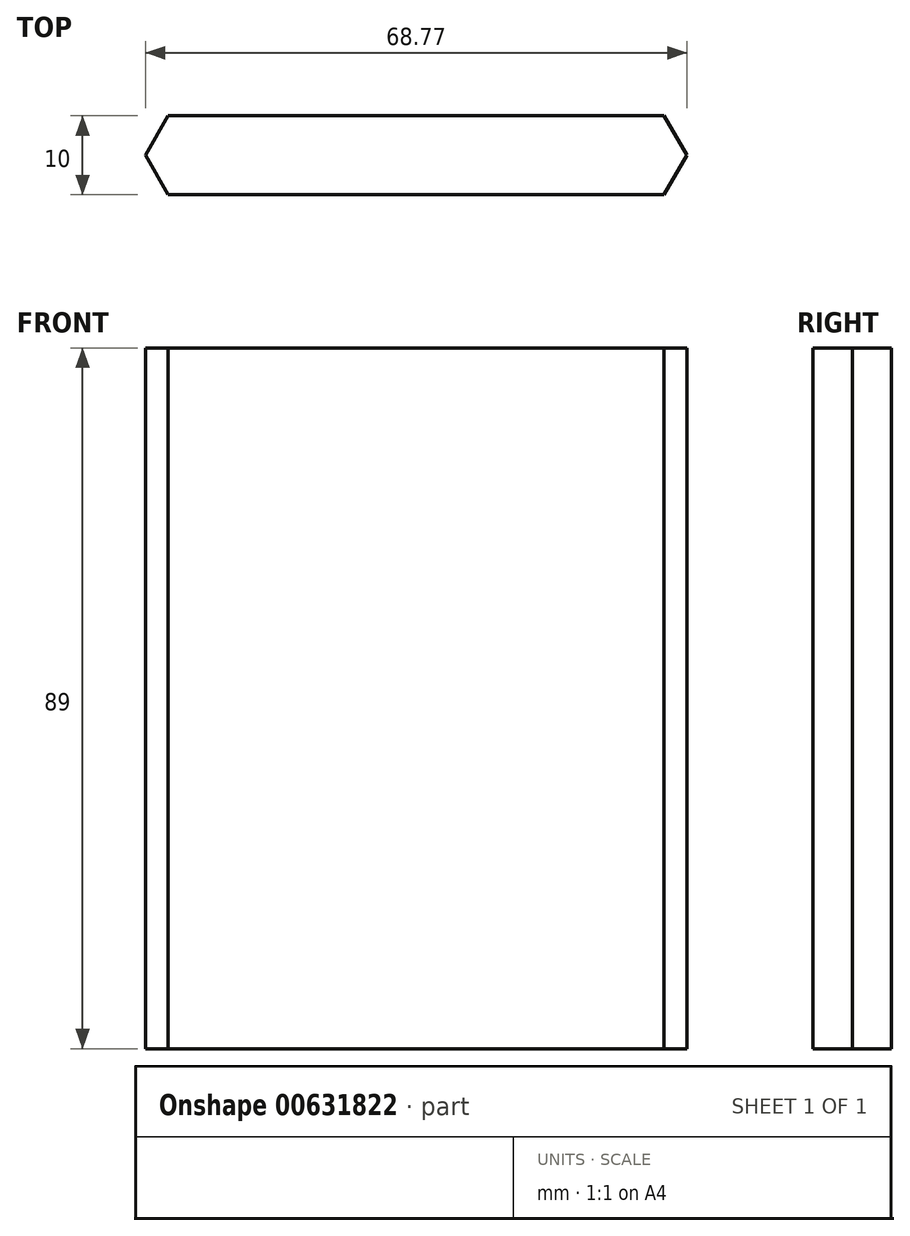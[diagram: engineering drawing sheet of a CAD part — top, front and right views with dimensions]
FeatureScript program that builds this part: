
annotation { "Feature Type Name" : "Feature", "Feature Type Description" : "" }
export const myFeature = defineFeature(function(context is Context, id is Id, definition is map)
    precondition{}
    {
        {
            var Q0;
            Q0=qCreatedBy(makeId("Top.planeOp"),FACE);
            var sketch = newSketch(context, id + "F0", { "sketchPlane" : qUnion([Q0])});
            skArc(sketch, "E0.cCircle", {"start": v(0, 5) * mm, "mid": v(-5, 0) * mm, "end": v(0, -5) * mm, "construction": true});
            skLineSegment(sketch, "E0.0", {"start": v(2.89, -5) * mm, "end": v(-2.89, -5) * mm});
            skLineSegment(sketch, "E0.1", {"start": v(-2.89, -5) * mm, "end": v(-5.77, 0) * mm});
            skLineSegment(sketch, "E0.2", {"start": v(-5.77, 0) * mm, "end": v(-2.89, 5) * mm});
            skLineSegment(sketch, "E0.3", {"start": v(-2.89, 5) * mm, "end": v(2.89, 5) * mm});
            skPoint(sketch, "E0.0.midPoint", {"position": v(0, -5) * mm});
            skLineSegment(sketch, "E1", {"start": v(-2.89, 5) * mm, "end": v(60.11, 5) * mm});
            skLineSegment(sketch, "E2", {"start": v(-2.89, -5) * mm, "end": v(60.11, -5) * mm});
            skArc(sketch, "E3.cCircle", {"start": v(57.23, -5) * mm, "mid": v(62.23, 0) * mm, "end": v(57.23, 5) * mm, "construction": true});
            skLineSegment(sketch, "E3.0", {"start": v(60.11, -5) * mm, "end": v(54.34, -5) * mm});
            skLineSegment(sketch, "E3.3", {"start": v(54.34, 5) * mm, "end": v(60.11, 5) * mm});
            skLineSegment(sketch, "E3.4", {"start": v(60.11, 5) * mm, "end": v(63, 0) * mm});
            skLineSegment(sketch, "E3.5", {"start": v(63, 0) * mm, "end": v(60.11, -5) * mm});
            skPoint(sketch, "E3.0.midPoint", {"position": v(57.23, -5) * mm});
            skPoint(sketch, "E4.orphan", {"position": v(5.77, 0) * mm});
            skPoint(sketch, "E5.orphan", {"position": v(51.45, 0) * mm});
            skSolve(sketch);
        }
        {
            var Q0;
            {var subQ1=sQuery(id+"F0.wireOp",EDGE,"E0.1");Q0=makeQuery(id+"F0.imprint","IMPRINT",FACE,{"disambiguationData":[TD([[makeQuery(id+"F0.imprint","IMPRINT",EDGE,{"derivedFrom":subQ1}),-1.0]])]});}
            extrude(context, id + "F1", {"entities" : qUnion([Q0]), "depth" : 89 * mm, "offsetDistance" : 25 * mm});
        }
    });
